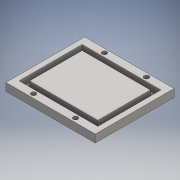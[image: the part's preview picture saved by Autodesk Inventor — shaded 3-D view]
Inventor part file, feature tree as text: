
AUTODESK INVENTOR PART (.ipt)
format: ipt  version: 2016 (Build 200138000, 138)  size: 123,392 bytes
history: native  units: mm
features: sketch x3, extrude x2, hole x1
ambient origin geometry x8: Origin, YZ Plane, XZ Plane, XY Plane, X Axis, Y Axis, Z Axis, Center Point
bodies: Solid1 (feature_tree)
feature tree (6):
  extrude  "Extrusion1"  Depth=75.0mm
  hole  "Hole1"  [1 undecoded]
  extrude  "Extrusion2"  Depth=6.0mm
  sketch  "Sketch1"  dims[d0=85.0mm d1=75.0mm]
  sketch  "Sketch2"  dims[d2=37.5mm d3=42.5mm]
  sketch  "Sketch3"  dims[d4=7.5mm d5=0.0mm d6=40.0mm d7=20.0mm d8=67.5mm d9=33.75mm d10=4.5mm d11=6.35mm d12=9.4mm d13=2.0mm d14=90.0deg d15=9.525mm d16=20.594885mm d19=75.0mm d22=60.0mm d23=30.0mm d24=5.0mm d26=37.5mm d27=5.0mm d29=5.0mm d30=5.0mm d31=6.0mm d32=0.0mm]
note: 1 required parameter value undecoded (feature->parameter linkage not recoverable at this tier; creation-order binding heuristic only, values carry confidence <= 0.55)
